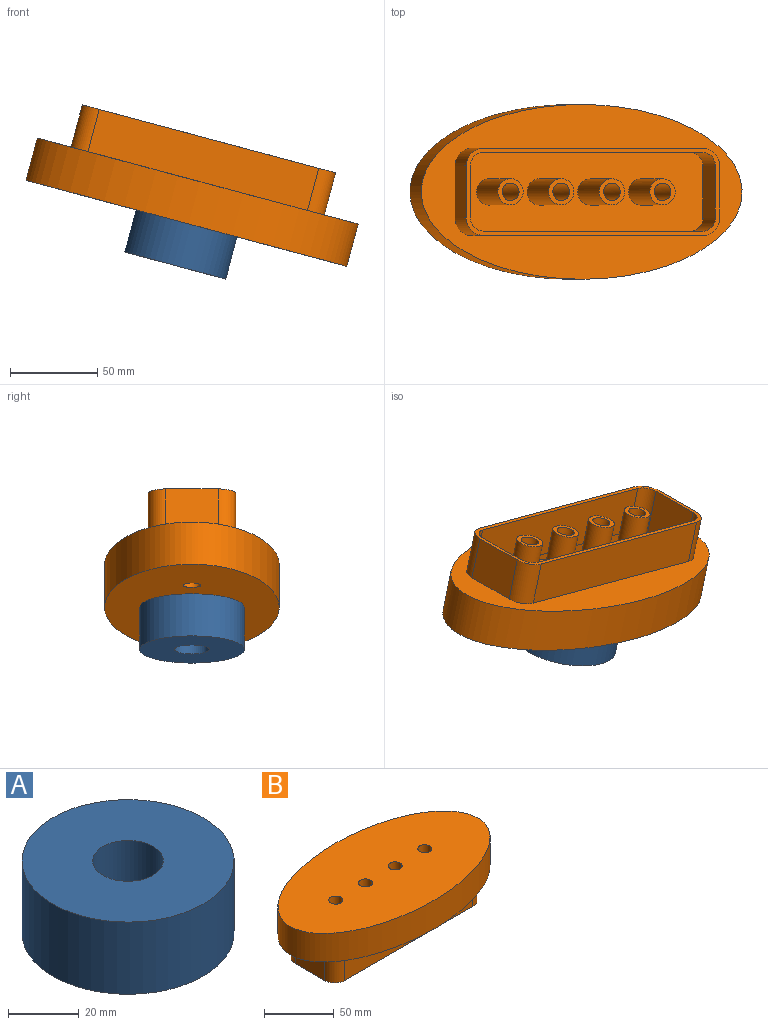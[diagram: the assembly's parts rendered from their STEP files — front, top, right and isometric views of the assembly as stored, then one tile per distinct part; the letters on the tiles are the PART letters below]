
ASSEMBLY  parts=2 mates=1
PART A: 4 faces, bbox 60x60x25 mm
  f0: cylinder r=10mm len=25mm, axis (0,0,-1), area 1570.8mm2, adj f2,f3
  f1: cylinder r=30mm len=60mm, axis (0,0,-1), area 4712.4mm2, adj f2,f3
  f2: plane 60x60mm, normal (0,0,1), area 2513.3mm2, adj f0,f1
  f3: plane 60x60mm, normal (0,0,-1), area 2513.3mm2, adj f0,f1
PART B: 35 faces, bbox 190x100x50 mm
  f0: plane 15x15mm, normal (0,0,-1), area 98.2mm2, adj f19,f34
  f1: plane 15x15mm, normal (0,0,-1), area 98.2mm2, adj f18,f33
  f2: plane 15x15mm, normal (0,0,-1), area 98.2mm2, adj f17,f32
  f3: plane 15x15mm, normal (0,0,-1), area 98.2mm2, adj f16,f31
  f4: plane 130x25mm, normal (0,-1,0), area 3250mm2, adj f8,f9,f12,f13
  f5: plane 30x25mm, normal (1,0,0), area 750mm2, adj f8,f9,f10,f13
  f6: plane 130x25mm, normal (0,1,0), area 3250mm2, adj f8,f10,f11,f13
  f7: plane 30x25mm, normal (-1,0,0), area 750mm2, adj f8,f11,f12,f13
  f8: plane 150x50mm, normal (0,0,-1), area 937.4mm2, adj f4,f5,f6,f7,f9,f10,f11,f12
  f9: cylinder r=10mm len=25mm, axis (0,0,-1), area 392.7mm2, adj f4,f5,f8,f13
  f10: cylinder r=10mm len=25mm, axis (0,0,-1), area 392.7mm2, adj f5,f6,f8,f13
  f11: cylinder r=10mm len=25mm, axis (0,0,-1), area 392.7mm2, adj f6,f7,f8,f13
  f12: cylinder r=10mm len=25mm, axis (0,0,-1), area 392.7mm2, adj f4,f7,f8,f13
  f13: plane 190x100mm, normal (0,0,-1), area 7508.4mm2, adj f4,f5,f6,f7,f9,f10,f11,f12
  f14: extruded ~190x100mm, area 11664.4mm2, adj f13,f15
  f15: plane 190x100mm, normal (0,0,1), area 14608.4mm2, adj f14,f16,f17,f18,f19
  f16: cylinder r=5mm len=50mm, axis (0,0,-1), area 1570.8mm2, adj f3,f15
  f17: cylinder r=5mm len=50mm, axis (0,0,-1), area 1570.8mm2, adj f2,f15
  f18: cylinder r=5mm len=50mm, axis (0,0,-1), area 1570.8mm2, adj f1,f15
  f19: cylinder r=5mm len=50mm, axis (0,0,-1), area 1570.8mm2, adj f0,f15
  f20: plane 130x27.5mm, normal (0,1,0), area 3575mm2, adj f8,f24,f27,f28
  f21: plane 30x27.5mm, normal (-1,0,0), area 825mm2, adj f8,f24,f25,f28
  f22: plane 130x27.5mm, normal (0,-1,0), area 3575mm2, adj f8,f25,f26,f28
  f23: plane 30x27.5mm, normal (1,0,0), area 825mm2, adj f8,f26,f27,f28
  f24: cylinder r=7.5mm len=27.5mm, axis (0,0,-1), area 324mm2, adj f8,f20,f21,f28
  f25: cylinder r=7.5mm len=27.5mm, axis (0,0,-1), area 324mm2, adj f8,f21,f22,f28
  f26: cylinder r=7.5mm len=27.5mm, axis (0,0,-1), area 324mm2, adj f8,f22,f23,f28
  f27: cylinder r=7.5mm len=27.5mm, axis (0,0,-1), area 324mm2, adj f8,f20,f23,f28
  f28: plane 185.01x95.02mm, normal (0,0,1), area 7297mm2, adj f20,f21,f22,f23,f24,f25,f26,f27
  f29: extruded ~185x95mm, area 9017.7mm2, adj f28,f30
  f30: plane 185.01x95.02mm, normal (0,0,-1), area 13066.9mm2, adj f29,f31,f32,f33,f34
  f31: cylinder r=7.5mm len=47.5mm, axis (0,0,-1), area 2238.4mm2, adj f3,f30
  f32: cylinder r=7.5mm len=47.5mm, axis (0,0,-1), area 2238.4mm2, adj f2,f30
  f33: cylinder r=7.5mm len=47.5mm, axis (0,0,-1), area 2238.4mm2, adj f1,f30
  f34: cylinder r=7.5mm len=47.5mm, axis (0,0,-1), area 2238.4mm2, adj f0,f30
PLACE A rot(axis=(0.99,0,-0.13),180deg) t=(14.61,-34.72,46.42)mm
PLACE B rot(axis=(0.99,0,-0.13),180deg) t=(27.55,-34.72,94.72)mm
MATE fastened A.f0 <-> B.f15  axis (0.26,0,0.97) through (14.61,-34.72,46.42)mm
